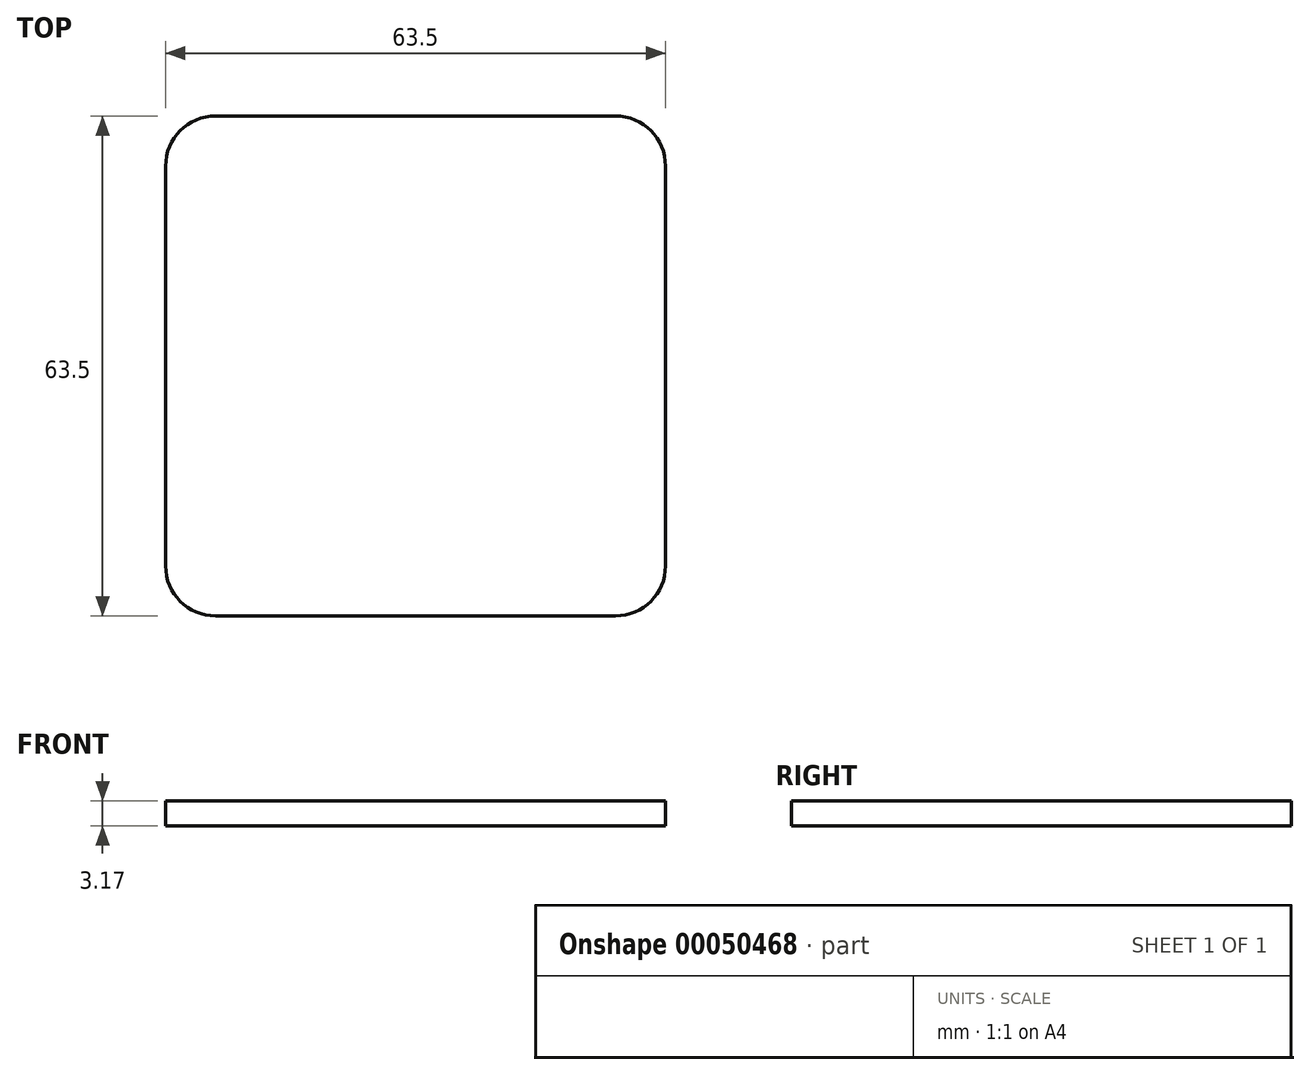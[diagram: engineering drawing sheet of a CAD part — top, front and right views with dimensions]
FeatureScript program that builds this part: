
annotation { "Feature Type Name" : "Feature", "Feature Type Description" : "" }
export const myFeature = defineFeature(function(context is Context, id is Id, definition is map)
    precondition{}
    {
        {
            var Q0;
            Q0=qCreatedBy(makeId("Top.planeOp"),FACE);
            var sketch = newSketch(context, id + "F0", { "sketchPlane" : qUnion([Q0])});
            skLineSegment(sketch, "E0.rect.bottom", {"start": v(-25.4, 31.75) * mm, "end": v(25.4, 31.75) * mm});
            skLineSegment(sketch, "E0.rect.top", {"start": v(-25.4, -31.75) * mm, "end": v(25.4, -31.75) * mm});
            skLineSegment(sketch, "E0.rect.left", {"start": v(-31.75, 25.4) * mm, "end": v(-31.75, -25.4) * mm});
            skLineSegment(sketch, "E0.rect.right", {"start": v(31.75, 25.4) * mm, "end": v(31.75, -25.4) * mm});
            skPoint(sketch, "E1.rect.middle", {"position": v(-31.75, 31.75) * mm});
            skPoint(sketch, "E2.orphan", {"position": v(-78.06, 4.98) * mm});
            skPoint(sketch, "E1.rect.top.end.orphan", {"position": v(-45.03, 52.94) * mm});
            skPoint(sketch, "E1.rect.right.start.orphan", {"position": v(14.56, 58.52) * mm});
            skArc(sketch, "E3.filletArc", {"start": v(-25.4, 31.75) * mm, "mid": v(-29.9, 29.9) * mm, "end": v(-31.75, 25.4) * mm});
            skPoint(sketch, "E4.visualSharp", {"position": v(-31.75, -31.75) * mm});
            skArc(sketch, "E4.filletArc", {"start": v(-31.75, -25.4) * mm, "mid": v(-29.9, -29.9) * mm, "end": v(-25.4, -31.75) * mm});
            skPoint(sketch, "E5.visualSharp", {"position": v(31.75, -31.75) * mm});
            skArc(sketch, "E5.filletArc", {"start": v(25.4, -31.75) * mm, "mid": v(29.9, -29.9) * mm, "end": v(31.75, -25.4) * mm});
            skPoint(sketch, "E6.visualSharp", {"position": v(31.75, 31.75) * mm});
            skArc(sketch, "E6.filletArc", {"start": v(31.75, 25.4) * mm, "mid": v(29.9, 29.9) * mm, "end": v(25.4, 31.75) * mm});
            skSolve(sketch);
        }
        {
            var Q0;
            Q0 = qSketchRegion(id + "F0", true);
            extrude(context, id + "F1", {"entities" : qUnion([Q0]), "depth" : 3.17 * mm});
        }
    });
